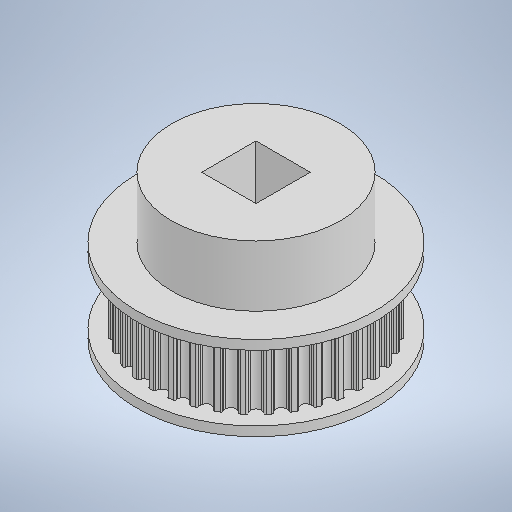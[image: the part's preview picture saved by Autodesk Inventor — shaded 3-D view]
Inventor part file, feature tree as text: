
AUTODESK INVENTOR PART (.ipt)
format: ipt  version: 2025.2 (Build 292293000, 293)  size: 844,800 bytes
history: native  units: mm
features: extrude x5, sketch x3, pattern_circular x1, mirror x1
ambient origin geometry x8: Origin, YZ Plane, XZ Plane, XY Plane, X Axis, Y Axis, Z Axis, Center Point
bodies: Solid1 (feature_tree)
feature tree (10):
  sketch  "Sketch1"  dims[d0=22.918312mm d1=0.872665mm]
  extrude  "Extrusion1"  Depth=0.872665mm
  extrude  "Extrusion2"  Depth=1.004mm
  extrude  "Extrusion3"  Depth=0.555mm
  pattern_circular  "Circular Pattern1"  [2 undecoded]
  mirror  "Mirror3"
  extrude  "Extrusion4"  Depth=0.15mm
  extrude  "Extrusion5"  Depth=4.5mm TaperAngle=0.0deg
  sketch  "Sketch2"  dims[d2=0.349066mm d4=1.004mm]
  sketch  "Sketch3"  dims[d13=0.75mm d14=0.555mm d15=1.0mm d16=0.15mm d18=4.5mm d19=0.0mm d20=3.5mm d21=0.0mm d22=3.5mm d23=0.0mm d24=360.0mm d25=360.0deg d28=0.0mm d29=0.0mm d33=7.5mm d34=0.0mm d35=25.4mm d36=18.0mm d37=5.8mm d38=5.8mm]
note: 2 required parameter values undecoded (feature->parameter linkage not recoverable at this tier; creation-order binding heuristic only, values carry confidence <= 0.55)
